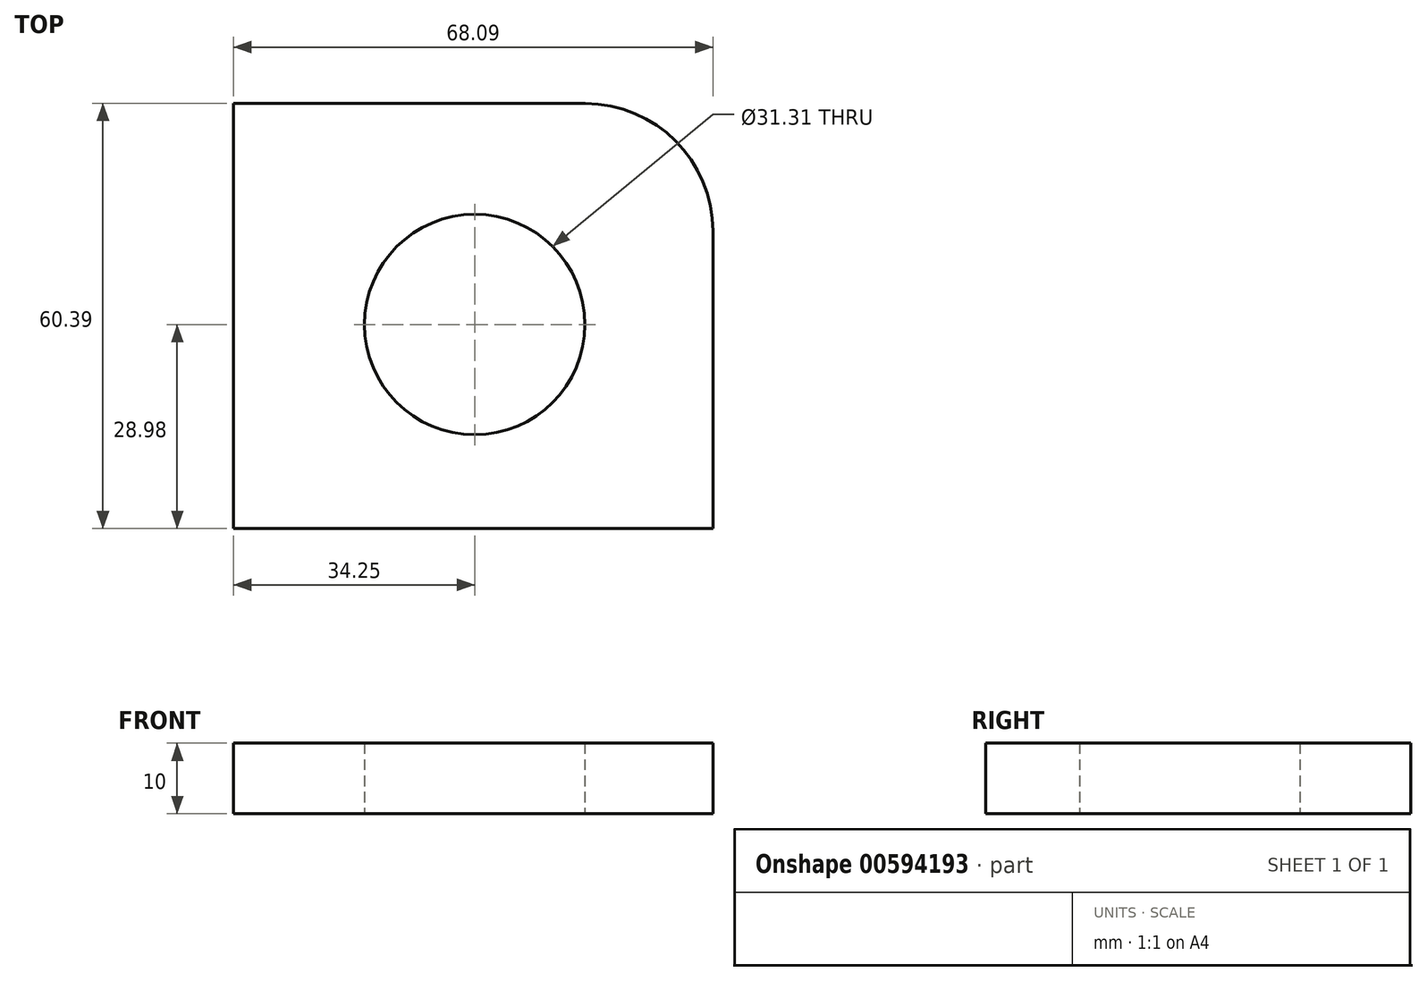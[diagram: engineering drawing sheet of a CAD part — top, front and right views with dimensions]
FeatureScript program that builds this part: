
annotation { "Feature Type Name" : "Feature", "Feature Type Description" : "" }
export const myFeature = defineFeature(function(context is Context, id is Id, definition is map)
    precondition{}
    {
        {
            var Q0;
            Q0=qCreatedBy(makeId("Top.planeOp"),FACE);
            var sketch = newSketch(context, id + "F0", { "sketchPlane" : qUnion([Q0])});
            skLineSegment(sketch, "E0.bottom", {"start": v(-34.25, 31.4) * mm, "end": v(15.67, 31.4) * mm});
            skLineSegment(sketch, "E0.top", {"start": v(-34.25, -28.98) * mm, "end": v(33.84, -28.98) * mm});
            skLineSegment(sketch, "E0.left", {"start": v(-34.25, 31.4) * mm, "end": v(-34.25, -28.98) * mm});
            skLineSegment(sketch, "E0.right", {"start": v(33.84, 13.24) * mm, "end": v(33.84, -28.98) * mm});
            skCircle(sketch, "E1", {"center": v(0, 0) * mm, "radius": 2.09 * mm});
            skCircle(sketch, "E2", {"center": v(0, 0) * mm, "radius": 15.65 * mm});
            skPoint(sketch, "E3.visualSharp", {"position": v(33.84, 31.4) * mm});
            skArc(sketch, "E3.filletArc", {"start": v(33.84, 13.24) * mm, "mid": v(28.52, 26.09) * mm, "end": v(15.67, 31.4) * mm});
            skSolve(sketch);
        }
        {
            var Q0;
            Q0=makeQuery(id+"F0.imprint","IMPRINT",FACE,{"disambiguationData":[TD([[makeQuery(id+"F0.imprint","IMPRINT",EDGE,{"derivedFrom":sQuery(id+"F0.wireOp",EDGE,"E0.bottom")}),-1.0]])]});
            extrude(context, id + "F1", {"entities" : qUnion([Q0]), "depth" : 10 * mm, "offsetDistance" : 25 * mm});
        }
    });
